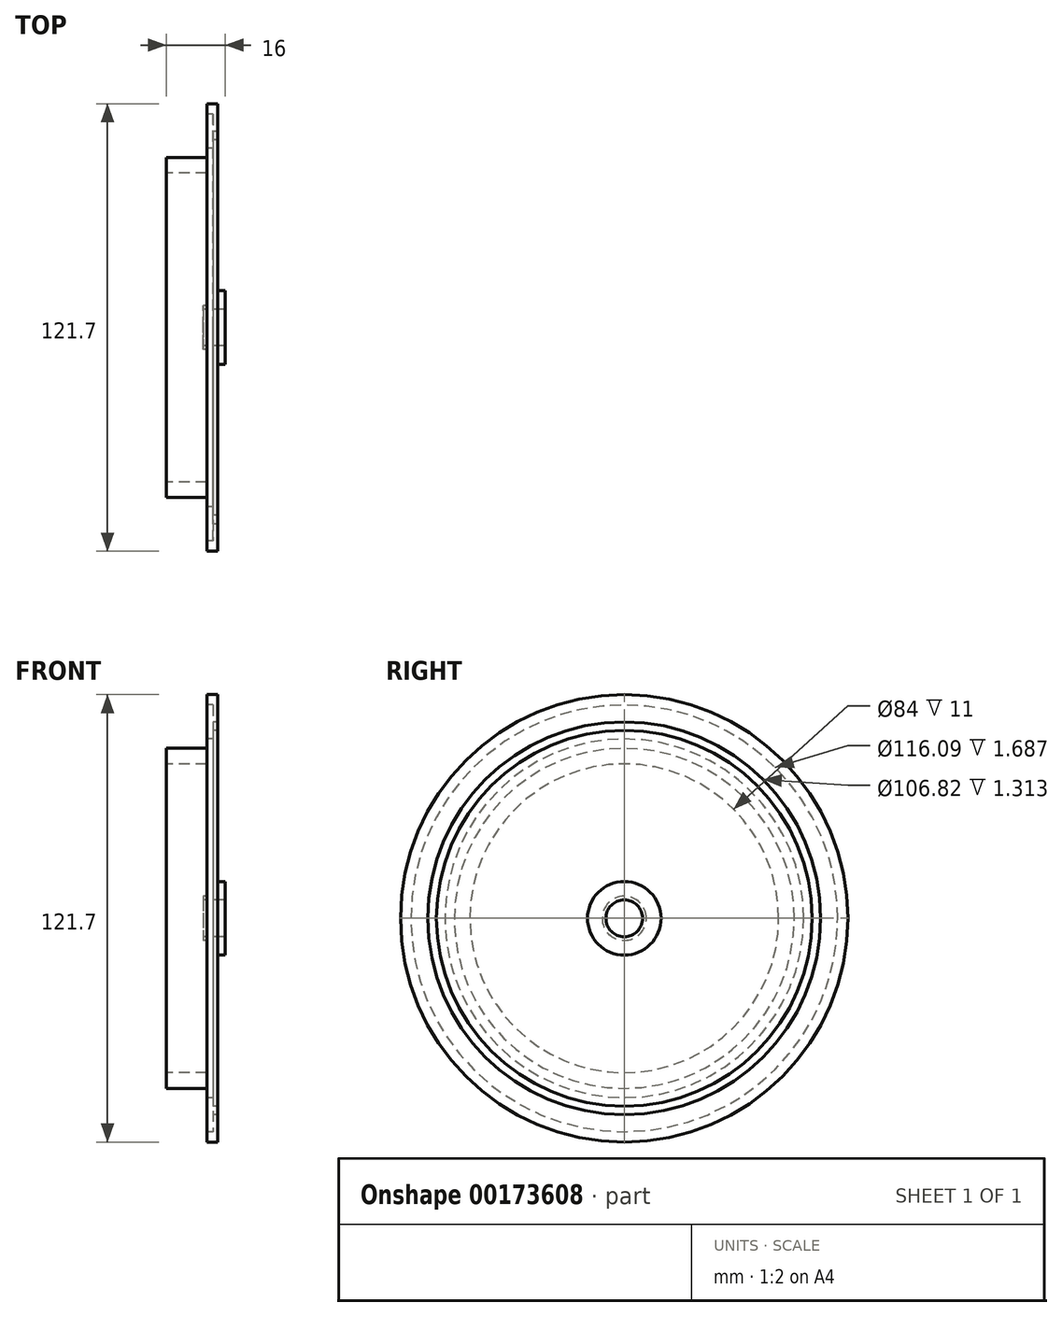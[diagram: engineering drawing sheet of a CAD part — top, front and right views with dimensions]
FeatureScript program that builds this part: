
annotation { "Feature Type Name" : "Feature", "Feature Type Description" : "" }
export const myFeature = defineFeature(function(context is Context, id is Id, definition is map)
    precondition{}
    {
        {
            var Q0;
            Q0=qCreatedBy(makeId("Front.planeOp"),FACE);
            var sketch = newSketch(context, id + "F0", { "sketchPlane" : qUnion([Q0])});
            skLineSegment(sketch, "E0", {"start": v(-34.28, 0) * mm, "end": v(40.16, 0) * mm, "construction": true});
            skLineSegment(sketch, "E1.bottom", {"start": v(-11, 0) * mm, "end": v(0, 0) * mm});
            skLineSegment(sketch, "E1.top", {"start": v(-11, 46.24) * mm, "end": v(0, 46.24) * mm});
            skLineSegment(sketch, "E1.left", {"start": v(-11, 42) * mm, "end": v(-11, 46.24) * mm});
            skLineSegment(sketch, "E1.right", {"start": v(0, 5) * mm, "end": v(0, 46.24) * mm});
            skLineSegment(sketch, "E2.bottom", {"start": v(0, 0) * mm, "end": v(3, 0) * mm});
            skLineSegment(sketch, "E2.top", {"start": v(0, 60.85) * mm, "end": v(3, 60.85) * mm});
            skLineSegment(sketch, "E2.left", {"start": v(0, 5) * mm, "end": v(0, 48.77) * mm});
            skLineSegment(sketch, "E2.right", {"start": v(3, 5) * mm, "end": v(3, 53.4) * mm});
            skLineSegment(sketch, "E3.bottom", {"start": v(0, 58.04) * mm, "end": v(1.69, 58.04) * mm});
            skLineSegment(sketch, "E3.top", {"start": v(0, 48.77) * mm, "end": v(1.69, 48.77) * mm});
            skLineSegment(sketch, "E3.right", {"start": v(1.69, 58.04) * mm, "end": v(1.69, 53.4) * mm});
            skLineSegment(sketch, "E4.bottom", {"start": v(1.69, 53.4) * mm, "end": v(3, 53.4) * mm});
            skLineSegment(sketch, "E4.top", {"start": v(1.69, 51.1) * mm, "end": v(3, 51.1) * mm});
            skLineSegment(sketch, "E5.bottom", {"start": v(3, 10) * mm, "end": v(5, 10) * mm});
            skLineSegment(sketch, "E5.top", {"start": v(3, 0) * mm, "end": v(5, 0) * mm});
            skLineSegment(sketch, "E5.left", {"start": v(3, 10) * mm, "end": v(3, 5) * mm});
            skLineSegment(sketch, "E5.right", {"start": v(5, 10) * mm, "end": v(5, 5) * mm});
            skLineSegment(sketch, "E6.top", {"start": v(0, 0) * mm, "end": v(-1, 0) * mm});
            skLineSegment(sketch, "E7.bottom", {"start": v(-1, 0) * mm, "end": v(0, 0) * mm});
            skLineSegment(sketch, "E7.top", {"start": v(-1, 6) * mm, "end": v(0, 6) * mm});
            skLineSegment(sketch, "E7.left", {"start": v(-1, 5) * mm, "end": v(-1, 6) * mm});
            skLineSegment(sketch, "E7.right", {"start": v(0, 5) * mm, "end": v(0, 6) * mm});
            skLineSegment(sketch, "E8.top", {"start": v(-11, 42) * mm, "end": v(0, 42) * mm});
            skLineSegment(sketch, "E8.left", {"start": v(-11, 46.24) * mm, "end": v(-11, 42) * mm});
            skLineSegment(sketch, "E8.right", {"start": v(0, 46.24) * mm, "end": v(0, 42) * mm});
            skLineSegment(sketch, "E9.trimOffspring", {"start": v(0, 58.04) * mm, "end": v(0, 60.85) * mm});
            skLineSegment(sketch, "E10.trimOffspring", {"start": v(1.69, 51.1) * mm, "end": v(1.69, 48.77) * mm});
            skLineSegment(sketch, "E11", {"start": v(-1, 5) * mm, "end": v(5, 5) * mm});
            skLineSegment(sketch, "E12.trimOffspring", {"start": v(3, 51.1) * mm, "end": v(3, 60.85) * mm});
            skLineSegment(sketch, "E13", {"start": v(0, 0) * mm, "end": v(0, 5) * mm});
            skSolve(sketch);
        }
        {
            var Q0;
            {var subQ2=sQuery(id+"F0.wireOp",EDGE,"E2.top");Q0=makeQuery(id+"F0.imprint","IMPRINT",FACE,{"disambiguationData":[TD([[makeQuery(id+"F0.imprint","IMPRINT",EDGE,{"derivedFrom":subQ2}),-1.0]])]});}
            var Q1;
            Q1=makeQuery(id+"F0.imprint","IMPRINT",FACE,{"disambiguationData":[TD([[makeQuery(id+"F0.imprint","IMPRINT",EDGE,{"derivedFrom":sQuery(id+"F0.wireOp",EDGE,"E7.top")}),-1.0]])]});
            var Q2;
            Q2=makeQuery(id+"F0.imprint","IMPRINT",FACE,{"disambiguationData":[TD([[makeQuery(id+"F0.imprint","IMPRINT",EDGE,{"derivedFrom":sQuery(id+"F0.wireOp",EDGE,"E2.right")}),1.0]])]});
            var Q3;
            Q3=makeQuery(id+"F0.imprint","IMPRINT",FACE,{"disambiguationData":[TD([[makeQuery(id+"F0.imprint","IMPRINT",EDGE,{"derivedFrom":sQuery(id+"F0.wireOp",EDGE,"E5.bottom")}),-1.0]])]});
            var Q4;
            Q4=makeQuery(id+"F0.imprint","IMPRINT",FACE,{"disambiguationData":[TD([[makeQuery(id+"F0.imprint","IMPRINT",EDGE,{"derivedFrom":sQuery(id+"F0.wireOp",EDGE,"E1.top")}),-1.0]])]});
            var Q5;
            Q5=sQuery(id+"F0.wireOp",EDGE,"E0");
            revolve(context, id + "F1", {"entities" : qUnion([Q0, Q1, Q2, Q3, Q4]), "axis" : qUnion([Q5]), "revolveType" : RevolveType.FULL});
        }
    });
